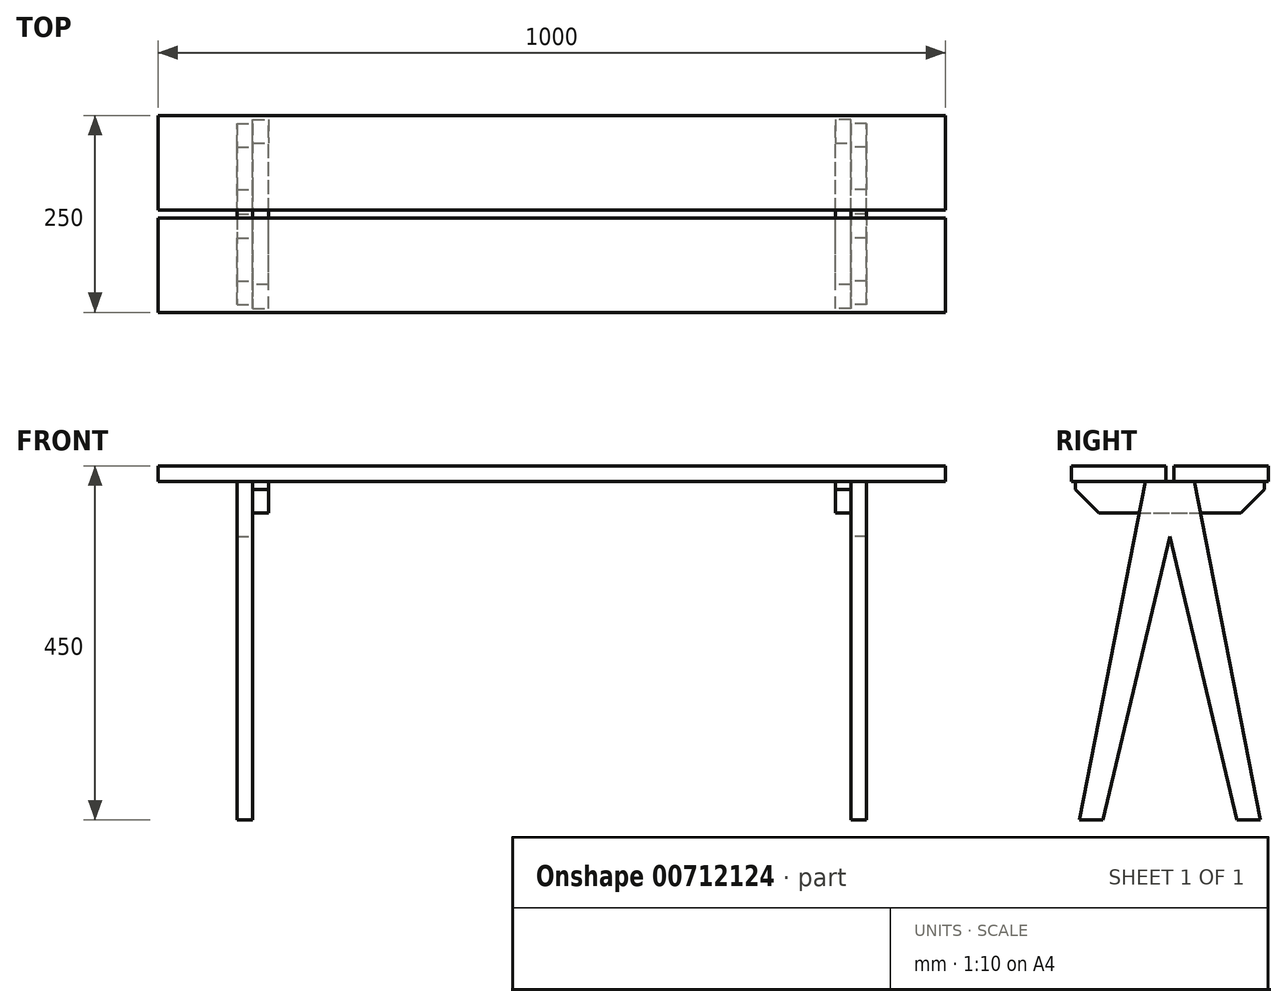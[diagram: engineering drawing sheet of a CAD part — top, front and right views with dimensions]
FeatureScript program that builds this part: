
annotation { "Feature Type Name" : "Feature", "Feature Type Description" : "" }
export const myFeature = defineFeature(function(context is Context, id is Id, definition is map)
    precondition{}
    {
        {
            var Q0;
            Q0=qCreatedBy(makeId("Top.planeOp"),FACE);
            var sketch = newSketch(context, id + "F0", { "sketchPlane" : qUnion([Q0])});
            skLineSegment(sketch, "E0.bottom", {"start": v(-500, 125) * mm, "end": v(500, 125) * mm});
            skLineSegment(sketch, "E0.top", {"start": v(-500, -125) * mm, "end": v(500, -125) * mm});
            skLineSegment(sketch, "E0.left", {"start": v(-500, 125) * mm, "end": v(-500, -125) * mm});
            skLineSegment(sketch, "E0.right", {"start": v(500, 125) * mm, "end": v(500, -125) * mm});
            skPoint(sketch, "E0.middle", {"position": v(0, 0) * mm});
            skLineSegment(sketch, "E1.bottom", {"start": v(-500, 5) * mm, "end": v(500, 5) * mm});
            skLineSegment(sketch, "E1.top", {"start": v(-500, -5) * mm, "end": v(500, -5) * mm});
            skLineSegment(sketch, "E1.left", {"start": v(-500, 5) * mm, "end": v(-500, -5) * mm});
            skLineSegment(sketch, "E1.right", {"start": v(500, 5) * mm, "end": v(500, -5) * mm});
            skSolve(sketch);
        }
        {
            var Q0;
            {var subQ0=sQuery(id+"F0.wireOp",EDGE,"E0.bottom");Q0=makeQuery(id+"F0.imprint","IMPRINT",FACE,{"disambiguationData":[TD([[makeQuery(id+"F0.imprint","IMPRINT",EDGE,{"derivedFrom":subQ0}),-1.0]])]});}
            var Q1;
            {var subQ0=sQuery(id+"F0.wireOp",EDGE,"E0.top");Q1=makeQuery(id+"F0.imprint","IMPRINT",FACE,{"disambiguationData":[TD([[makeQuery(id+"F0.imprint","IMPRINT",EDGE,{"derivedFrom":subQ0}),1.0]])]});}
            extrude(context, id + "F1", {"entities" : qUnion([Q0, Q1]), "depth" : 20 * mm, "offsetDistance" : 25 * mm});
        }
        {
            var Q0;
            Q0=qCreatedBy(makeId("Front.planeOp"),FACE);
            var sketch = newSketch(context, id + "F2", { "sketchPlane" : qUnion([Q0])});
            skLineSegment(sketch, "E2", {"start": v(0, 66.67) * mm, "end": v(0, -64.95) * mm});
            skLineSegment(sketch, "E3.bottom", {"start": v(-380, 0) * mm, "end": v(-360, 0) * mm});
            skLineSegment(sketch, "E3.top", {"start": v(-380, -40) * mm, "end": v(-360, -40) * mm});
            skLineSegment(sketch, "E3.left", {"start": v(-380, 0) * mm, "end": v(-380, -40) * mm});
            skLineSegment(sketch, "E3.right", {"start": v(-360, 0) * mm, "end": v(-360, -40) * mm});
            skLineSegment(sketch, "E4.MirrorCS", {"start": v(380, 0) * mm, "end": v(380, -40) * mm});
            skLineSegment(sketch, "E5.MirrorCS", {"start": v(380, 0) * mm, "end": v(360, 0) * mm});
            skLineSegment(sketch, "E6.MirrorCS", {"start": v(360, 0) * mm, "end": v(360, -40) * mm});
            skLineSegment(sketch, "E7.MirrorCS", {"start": v(380, -40) * mm, "end": v(360, -40) * mm});
            skSolve(sketch);
        }
        {
            var Q0;
            Q0 = qSketchRegion(id + "F2", true);
            extrude(context, id + "F3", {"entities" : qUnion([Q0]), "endBound" : BoundingType.SYMMETRIC, "depth" : 240 * mm, "offsetDistance" : 25 * mm});
        }
        {
            var Q0;
            Q0=qCreatedBy(makeId("Right.planeOp"),FACE);
            var sketch = newSketch(context, id + "F4", { "sketchPlane" : qUnion([Q0])});
            skLineSegment(sketch, "E8", {"start": v(0, 0) * mm, "end": v(0, -70) * mm});
            skLineSegment(sketch, "E9", {"start": v(0, -70) * mm, "end": v(-85, -430) * mm});
            skLineSegment(sketch, "E10", {"start": v(-85, -430) * mm, "end": v(-115, -430) * mm});
            skLineSegment(sketch, "E11", {"start": v(-115, -430) * mm, "end": v(-30.93, 0) * mm});
            skLineSegment(sketch, "E12", {"start": v(-30.93, 0) * mm, "end": v(0, 0) * mm});
            skLineSegment(sketch, "E13", {"start": v(0, 72.77) * mm, "end": v(0, -79.95) * mm});
            skLineSegment(sketch, "E14.MirrorCS", {"start": v(30.93, 0) * mm, "end": v(0, 0) * mm});
            skLineSegment(sketch, "E15.MirrorCS", {"start": v(115, -430) * mm, "end": v(30.93, 0) * mm});
            skLineSegment(sketch, "E16.MirrorCS", {"start": v(85, -430) * mm, "end": v(115, -430) * mm});
            skLineSegment(sketch, "E17.MirrorCS", {"start": v(0, -70) * mm, "end": v(85, -430) * mm});
            skSolve(sketch);
        }
        {
            var Q0;
            Q0 = qSketchRegion(id + "F4", true);
            extrude(context, id + "F5", {"entities" : qUnion([Q0]), "depth" : 400 * mm, "offsetDistance" : 25 * mm, "hasSecondDirection" : true, "secondDirectionOppositeDirection" : false, "secondDirectionDepth" : 380 * mm});
        }
        {
            var Q0;
            {var subQ0=sQuery(id+"F4.wireOp",EDGE,"E14.MirrorCS");Q0=makeQuery(id+"F4.imprint","IMPRINT",FACE,{"disambiguationData":[TD([[makeQuery(id+"F4.imprint","IMPRINT",EDGE,{"derivedFrom":subQ0}),1.0]])]});}
            var Q1;
            {var subQ1=sQuery(id+"F4.wireOp",EDGE,"E9");Q1=makeQuery(id+"F4.imprint","IMPRINT",FACE,{"disambiguationData":[TD([[makeQuery(id+"F4.imprint","IMPRINT",EDGE,{"derivedFrom":subQ1}),-1.0]])]});}
            extrude(context, id + "F6", {"entities" : qUnion([Q0, Q1]), "oppositeDirection" : true, "depth" : 400 * mm, "offsetDistance" : 25 * mm, "hasSecondDirection" : true, "secondDirectionOppositeDirection" : true, "secondDirectionDepth" : 380 * mm});
        }
        {
            var Q0;
            Q0=makeQuery(id+"F3.opExtrude","CAP_EDGE",EDGE,{"disambiguationData":[OSD([sQuery(id+"F2.wireOp",EDGE,"E3.top")])],"isStart":false});
            var Q1;
            Q1=makeQuery(id+"F3.opExtrude","CAP_EDGE",EDGE,{"disambiguationData":[OSD([sQuery(id+"F2.wireOp",EDGE,"E7.MirrorCS")])],"isStart":false});
            var Q2;
            Q2=makeQuery(id+"F3.opExtrude","CAP_EDGE",EDGE,{"disambiguationData":[OSD([sQuery(id+"F2.wireOp",EDGE,"E7.MirrorCS")])],"isStart":true});
            var Q3;
            Q3=makeQuery(id+"F3.opExtrude","CAP_EDGE",EDGE,{"disambiguationData":[OSD([sQuery(id+"F2.wireOp",EDGE,"E3.top")])],"isStart":true});
            chamfer(context, id + "F7", {"entities" : qUnion([Q0, Q1, Q2, Q3]), "width" : 30 * mm, "tangentPropagation" : true});
        }
    });
